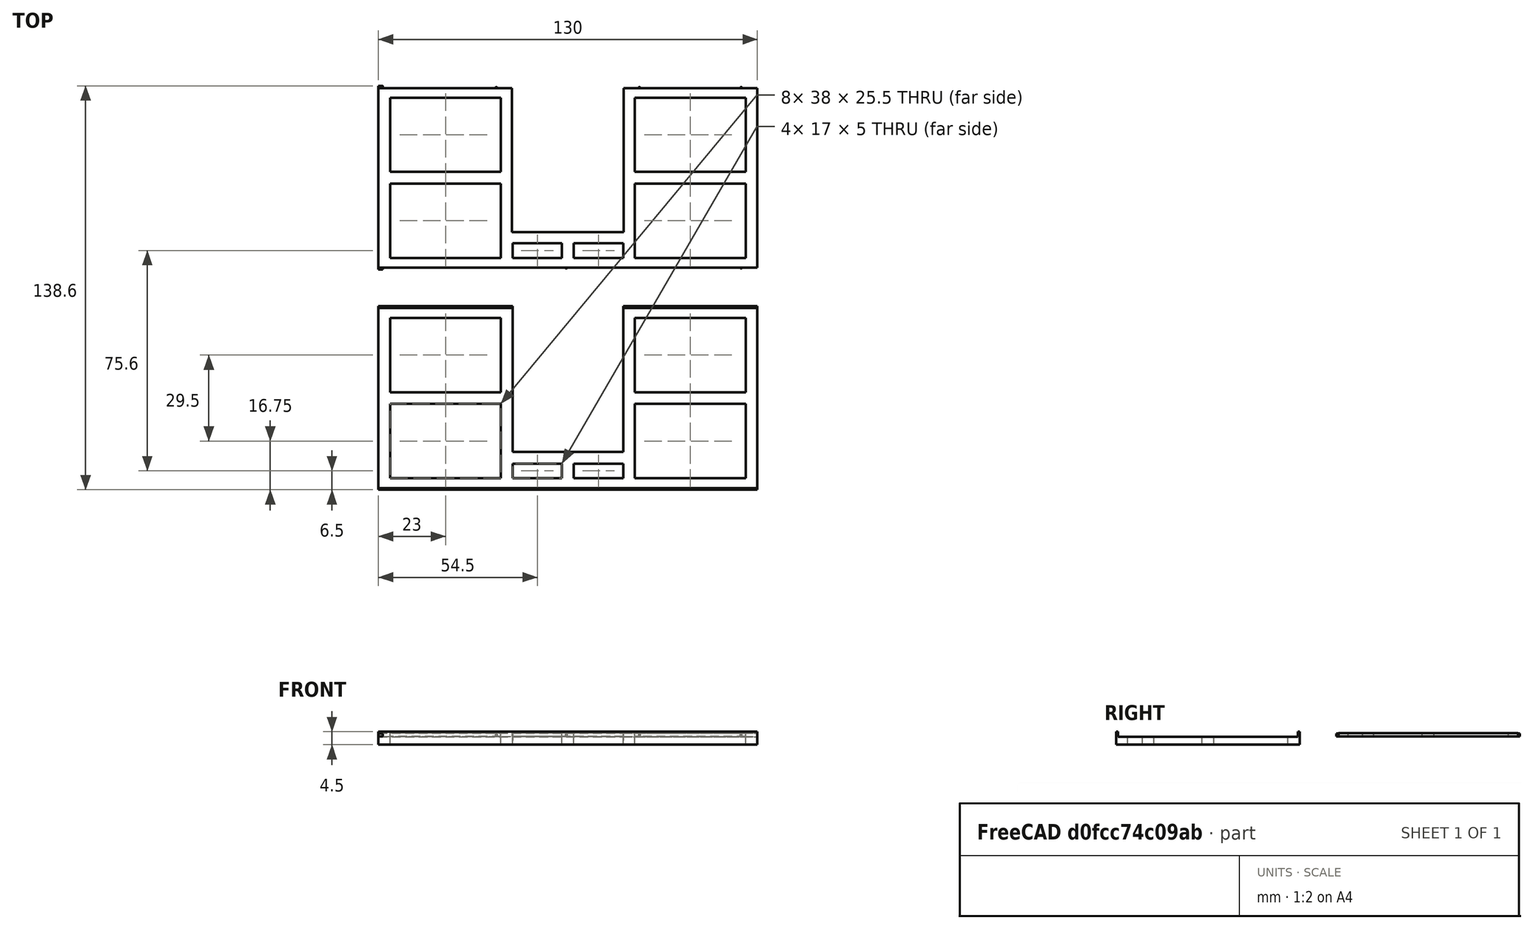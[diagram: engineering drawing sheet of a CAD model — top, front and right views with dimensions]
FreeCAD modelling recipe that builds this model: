
FCSTD DOCUMENT  (FreeCAD 0.18R)
Label: plustek120_tray
License: All rights reserved
LicenseURL: http://en.wikipedia.org/wiki/All_rights_reserved
objects: Part::Box×13, Part::MultiFuse×7, Part::Sphere×5, Part::Cut×4, Part::Cylinder×2, Spreadsheet::Sheet×1, App::Part×1
note: 31 computed .brp shape members not serialized (recipe doc carries the construction recipe); baked Part::Feature solids carry a one-line shape summary decoded from their .brp

FEATURE [Part::Box] Box  label="basebox"
  AttacherType = Attacher::AttachEngine3D
  Height = 4.5
  Length = 130
  Width = 63
  expr: Height = dims.baseheight
  expr: Width = dims.basewidth
  expr: Length = dims.baselength
FEATURE [Part::Box] Box001  label="filmcutaway"
  AttacherType = Attacher::AttachEngine3D
  Height = 5.5
  Length = 132
  Placement = pos=(-1,0.6,2.7) rot=(0,0,1;0rad)
  Width = 61.8
  expr: Width = dims.filmheight
  expr: Height = dims.baseheight + dims.overcut
  expr: Placement.Base.z = dims.filmplane
  expr: Placement.Base.y = (dims.basewidth - dims.filmheight) / 2
  expr: Placement.Base.x = -dims.overcut
  expr: Length = dims.baselength + dims.overcut * 2
FEATURE [Spreadsheet::Sheet] Spreadsheet  label="dims"
  cells = A1=basewidth; B1(basewidth)==63mm; D1=overcut; E1(overcut)==1mm; A2=baselength; B2(baselength)==130mm; A3=baseheight; B3(baseheight)==4.5mm; A4=filmplane; B4(filmplane)==2.7000000000000002mm; A5=filmheight; B5(filmheight)==61.799999999999997mm; A6=windowwidth; B6(windowwidth)==38mm; A7=windowheight; B7(windowheight)==50mm; A8=coverheight; B8(coverheight)==1.2mm; A9=hingerad; B9(hingerad)==0.5mm; A10=hingedepth; B10(hingedepth)==0.5mm; A11=inset; B11(inset)==0.10000000000000001mm; A12=filmthickness; B12(filmthickness)==0.10000000000000001mm; A13=clipgap; B13(clipgap)==5mm; A14=border; B14(border)==4mm
FEATURE [Part::Box] Box002  label="windowcutaway"
  AttacherType = Attacher::AttachEngine3D
  Height = 6.5
  Length = 38
  Placement = pos=(46,13,-1) rot=(0,0,1;0rad)
  Width = 51
  expr: Placement.Base.y = dims.basewidth - dims.windowheight
  expr: Placement.Base.x = dims.baselength / 2 - dims.windowwidth / 2
  expr: Placement.Base.z = -dims.overcut
  expr: Height = dims.baseheight + 2 * dims.overcut
  expr: Length = dims.windowwidth
  expr: Width = dims.windowheight + dims.overcut
FEATURE [Part::Box] Box003  label="coverbox"
  AttacherType = Attacher::AttachEngine3D
  Height = 1.2
  Length = 130
  Placement = pos=(0,0.7,2.7) rot=(0,0,1;0rad)
  Width = 61.6
  expr: Width = dims.filmheight - dims.inset * 2
  expr: Height = dims.coverheight
  expr: Placement.Base.z = dims.filmplane
  expr: Placement.Base.y = (dims.basewidth + dims.inset * 2 - dims.filmheight) / 2
  expr: Placement.Base.x = 0
  expr: Length = dims.baselength
FEATURE [Part::Box] Box004  label="coverwindowcutaway"
  AttacherType = Attacher::AttachEngine3D
  Height = 8
  Length = 38.4
  Placement = pos=(45.8,12.8,-1) rot=(0,0,1;0rad)
  Width = 50.2
  expr: Placement.Base.y = dims.basewidth - dims.windowheight - 2 * dims.inset
  expr: Placement.Base.x = (dims.baselength - dims.windowwidth - 4 * dims.inset) / 2
  expr: Placement.Base.z = -dims.overcut
  expr: Length = dims.windowwidth + 4 * dims.inset
  expr: Width = dims.windowheight + 2 * dims.inset
FEATURE [Part::Cut] Cut001  label="coverbase"
  Base = -> Box003
  Placement = pos=(0,0,0.1) rot=(0,0,1;0rad)
  Tool = -> Box004
  expr: Placement.Base.z = dims.filmthickness
FEATURE [Part::Cylinder] Cylinder
  Angle = 360
  AttacherType = Attacher::AttachEngine3D
  Height = 63
  Placement = pos=(1,63,3.3) rot=(1,0,0;1.5708rad)
  Radius = 0.5
  expr: Placement.Base.x = dims.hingerad + dims.hingedepth
  expr: Placement.Base.y = dims.basewidth
  expr: Placement.Base.z = dims.filmplane + dims.hingerad + dims.filmthickness
  expr: Height = dims.basewidth
  expr: Radius = dims.hingerad
FEATURE [Part::Box] Box005  label="Cube"
  AttacherType = Attacher::AttachEngine3D
  Height = 1
  Length = 1
  Placement = pos=(0,0,2.8) rot=(0,0,1;0rad)
  Width = 63
  expr: Placement.Base.x = -dims.hingerad + dims.hingedepth
  expr: Length = dims.hingedepth + dims.hingerad
  expr: Placement.Base.z = dims.filmplane + dims.filmthickness
  expr: Height = dims.hingerad * 2
  expr: Width = dims.basewidth
FEATURE [Part::Box] Box006  label="Cube001"
  AttacherType = Attacher::AttachEngine3D
  Height = 1
  Length = 1.5
  Placement = pos=(-0.5,-1,2.8) rot=(0,0,1;0rad)
  Width = 65
  expr: Placement.Base.y = -dims.overcut
  expr: Placement.Base.x = -dims.overcut + dims.hingerad
  expr: Length = dims.hingedepth + dims.overcut
  expr: Placement.Base.z = dims.filmplane + dims.filmthickness
  expr: Height = dims.hingerad * 2
  expr: Width = dims.basewidth + 2 * dims.overcut
FEATURE [Part::Cylinder] Cylinder001
  Angle = 360
  AttacherType = Attacher::AttachEngine3D
  Height = 65
  Placement = pos=(1,64,3.3) rot=(1,0,0;1.5708rad)
  Radius = 0.5
  expr: Placement.Base.x = dims.hingerad + dims.hingedepth
  expr: Placement.Base.y = dims.basewidth + dims.overcut
  expr: Placement.Base.z = dims.filmplane + dims.hingerad + dims.filmthickness
  expr: Height = dims.basewidth + 2 * dims.overcut
  expr: Radius = dims.hingerad
FEATURE [Part::MultiFuse] Fusion001  label="coverhinge"
  Shapes = -> [Cylinder,Box005]
FEATURE [Part::MultiFuse] Fusion002  label="coverhingecutaway"
  Shapes = -> [Box006,Cylinder001]
FEATURE [Part::Sphere] Sphere
  Angle1 = -90
  Angle2 = 90
  Angle3 = 360
  AttacherType = Attacher::AttachEngine3D
  Placement = pos=(124.45,0.8,3.35) rot=(0,0,1;0rad)
  Radius = 0.4
  expr: Placement.Base.y = dims.inset + dims.inset + (dims.basewidth - dims.filmheight) / 2
  expr: Placement.Base.x = dims.baselength - dims.hingerad - dims.inset / 2 - dims.clipgap
  expr: Placement.Base.z = dims.filmplane + dims.filmthickness + dims.hingerad + dims.inset / 2
  expr: Radius = dims.hingerad - dims.inset
FEATURE [Part::Sphere] Sphere001
  Angle1 = -90
  Angle2 = 90
  Angle3 = 360
  AttacherType = Attacher::AttachEngine3D
  Placement = pos=(64.45,0.8,3.35) rot=(0,0,1;0rad)
  Radius = 0.4
  expr: Placement.Base.y = dims.inset * 2 + (dims.basewidth - dims.filmheight) / 2
  expr: Placement.Base.x = dims.baselength / 2 - dims.hingerad - dims.inset / 2
  expr: Placement.Base.z = dims.filmplane + dims.filmthickness + dims.hingerad + dims.inset / 2
  expr: Radius = dims.hingerad - dims.inset
FEATURE [Part::Sphere] Sphere002
  Angle1 = -90
  Angle2 = 90
  Angle3 = 360
  AttacherType = Attacher::AttachEngine3D
  Placement = pos=(124.45,62.2,3.35) rot=(0,0,1;0rad)
  Radius = 0.4
  expr: Placement.Base.y = dims.hingerad + dims.filmheight - dims.inset
  expr: Placement.Base.x = dims.baselength - dims.hingerad - dims.inset / 2 - dims.clipgap
  expr: Placement.Base.z = dims.filmplane + dims.filmthickness + dims.hingerad + dims.inset / 2
  expr: Radius = dims.hingerad - dims.inset
FEATURE [Part::Sphere] Sphere003
  Angle1 = -90
  Angle2 = 90
  Angle3 = 360
  AttacherType = Attacher::AttachEngine3D
  Placement = pos=(40.45,62.2,3.35) rot=(0,0,1;0rad)
  Radius = 0.4
  expr: Placement.Base.y = dims.hingerad + dims.filmheight - dims.inset
  expr: Placement.Base.x = dims.baselength / 2 - dims.windowwidth / 2 - dims.hingerad - dims.inset / 2 - dims.clipgap
  expr: Placement.Base.z = dims.filmplane + dims.filmthickness + dims.hingerad + dims.inset / 2
  expr: Radius = dims.hingerad - dims.inset
FEATURE [Part::Sphere] Sphere004
  Angle1 = -90
  Angle2 = 90
  Angle3 = 360
  AttacherType = Attacher::AttachEngine3D
  Placement = pos=(89.55,62.2,3.35) rot=(0,0,1;0rad)
  Radius = 0.4
  expr: Placement.Base.y = dims.hingerad + dims.filmheight - dims.inset
  expr: Placement.Base.x = dims.baselength / 2 + dims.windowwidth / 2 + dims.hingerad + dims.inset / 2 + dims.clipgap
  expr: Placement.Base.z = dims.filmplane + dims.filmthickness + dims.hingerad + dims.inset / 2
  expr: Radius = dims.hingerad - dims.inset
FEATURE [Part::MultiFuse] Fusion  label="hingeclips"
  Shapes = -> [Sphere,Sphere001,Sphere002,Sphere003,Sphere004]
FEATURE [Part::MultiFuse] Fusion003  label="cover"
  Shapes = -> [Fusion001,Fusion,Cut001]
  expr: Placement.Base.z = 0
  expr: Placement.Base.y = 0
FEATURE [Part::MultiFuse] Fusion004  label="hingeclips001"
  Shapes = -> [Sphere,Sphere001,Sphere002,Sphere003,Sphere004]
FEATURE [Part::MultiFuse] Fusion005
  Shapes = -> [Box001,Box002,Fusion002,Fusion004]
FEATURE [Part::Cut] Cut  label="base"
  Base = -> Box
  Tool = -> Fusion005
FEATURE [Part::Box] Box008  label="Cube003"
  AttacherType = Attacher::AttachEngine3D
  Height = 7.7
  Length = 38
  Placement = pos=(88,4,-1) rot=(0,0,1;0rad)
  Width = 25.5
  expr: Placement.Base.z = -dims.overcut
  expr: Height = dims.baseheight + dims.overcut * 2 + dims.coverheight
  expr: Placement.Base.y = dims.border
  expr: Placement.Base.x = dims.border + dims.baselength - (dims.baselength - dims.windowwidth) / 2
  expr: Length = (dims.baselength - dims.windowwidth) / 2 - dims.border * 2
  expr: Width = dims.basewidth / 2 - dims.border * 1.5
FEATURE [Part::Box] Box007  label="Cube002"
  AttacherType = Attacher::AttachEngine3D
  Height = 7.7
  Length = 38
  Placement = pos=(4,4,-1) rot=(0,0,1;0rad)
  Width = 25.5
  expr: Placement.Base.z = -dims.overcut
  expr: Height = dims.baseheight + dims.coverheight + dims.overcut * 2
  expr: Placement.Base.y = dims.border
  expr: Placement.Base.x = dims.border
  expr: Length = (dims.baselength - dims.windowwidth) / 2 - dims.border * 2
  expr: Width = dims.basewidth / 2 - dims.border * 1.5
FEATURE [Part::Box] Box009  label="Cube004"
  AttacherType = Attacher::AttachEngine3D
  Height = 7.7
  Length = 38
  Placement = pos=(4,33.5,-1) rot=(0,0,1;0rad)
  Width = 25.5
  expr: Placement.Base.z = -dims.overcut
  expr: Height = dims.baseheight + dims.coverheight + dims.overcut * 2
  expr: Placement.Base.y = dims.border / 2 + dims.basewidth / 2
  expr: Placement.Base.x = dims.border
  expr: Length = (dims.baselength - dims.windowwidth) / 2 - dims.border * 2
  expr: Width = dims.basewidth / 2 - dims.border * 1.5
FEATURE [Part::Box] Box010  label="Cube005"
  AttacherType = Attacher::AttachEngine3D
  Height = 7.7
  Length = 38
  Placement = pos=(88,33.5,-1) rot=(0,0,1;0rad)
  Width = 25.5
  expr: Placement.Base.z = -dims.overcut
  expr: Height = dims.baseheight + dims.overcut * 2 + dims.coverheight
  expr: Placement.Base.y = dims.border / 2 + dims.basewidth / 2
  expr: Placement.Base.x = dims.border + dims.baselength - (dims.baselength - dims.windowwidth) / 2
  expr: Length = (dims.baselength - dims.windowwidth) / 2 - dims.border * 2
  expr: Width = dims.basewidth / 2 - dims.border * 1.5
FEATURE [Part::Box] Box011  label="Cube006"
  AttacherType = Attacher::AttachEngine3D
  Height = 7.7
  Length = 17
  Placement = pos=(46,4,-1) rot=(0,0,1;0rad)
  Width = 5
  expr: Placement.Base.y = dims.border
  expr: Placement.Base.x = dims.baselength / 2 - dims.windowwidth / 2
  expr: Placement.Base.z = -dims.overcut
  expr: Height = dims.baseheight + dims.overcut * 2 + dims.coverheight
  expr: Width = dims.basewidth - dims.windowheight - dims.border * 2
  expr: Length = dims.windowwidth / 2 - dims.border / 2
FEATURE [Part::Box] Box012  label="Cube007"
  AttacherType = Attacher::AttachEngine3D
  Height = 7.7
  Length = 17
  Placement = pos=(67,4,-1) rot=(0,0,1;0rad)
  Width = 5
  expr: Placement.Base.y = dims.border
  expr: Placement.Base.x = dims.baselength / 2 - dims.windowwidth / 2 + dims.windowwidth / 2 + dims.border / 2
  expr: Placement.Base.z = -dims.overcut
  expr: Height = dims.baseheight + dims.overcut * 2 + dims.coverheight
  expr: Width = dims.basewidth - dims.windowheight - dims.border * 2
  expr: Length = dims.windowwidth / 2 - dims.border / 2
FEATURE [Part::MultiFuse] Fusion006  label="cutaway"
  Shapes = -> [Box007,Box010,Box009,Box012,Box011,Box008]
FEATURE [App::Part] Part  label="filmtray"
  Group = -> [Box,Box001,Spreadsheet,Box002,Box003,Box004,Cut001,Cylinder,Box005,Box006,Cylinder001,Fusion001,Fusion002,Sphere,Sphere001,Sphere002,Sphere003,Sphere004,Fusion,Fusion003,Fusion004,Fusion005,Cut,Box007,Box008,Box009,Box010,Box011,Box012,Fusion006]
  Origin = -> Origin
FEATURE [Part::Cut] Cut002  label="cutcover"
  Base = -> Fusion003
  Placement = pos=(0,75.6,0) rot=(0,0,1;0rad)
  Tool = -> Fusion006
  expr: Placement.Base.z = 0
  expr: Placement.Base.y = 1.2 * dims.basewidth
FEATURE [Part::Cut] Cut003
  Base = -> Cut
  Tool = -> Fusion006
